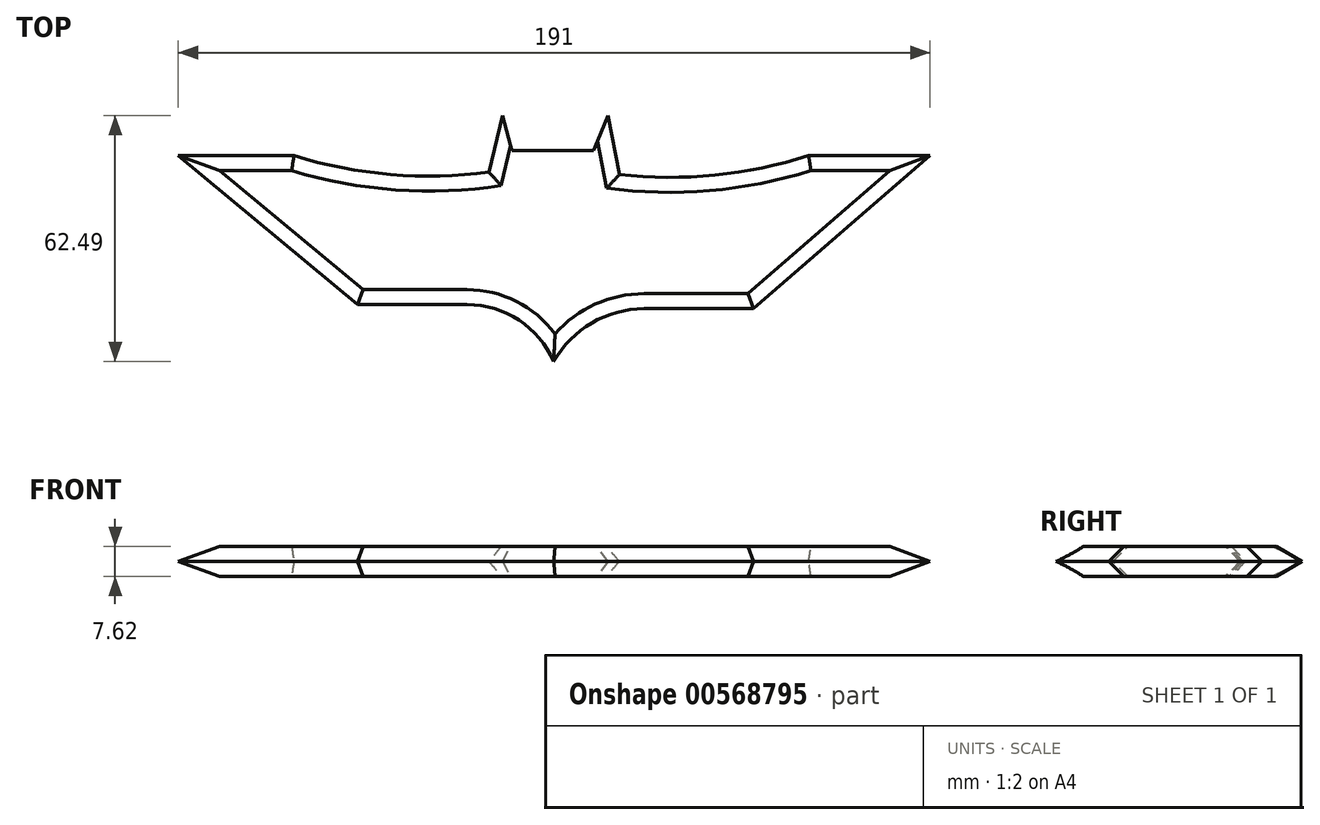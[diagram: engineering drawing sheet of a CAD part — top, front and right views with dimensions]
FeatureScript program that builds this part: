
annotation { "Feature Type Name" : "Feature", "Feature Type Description" : "" }
export const myFeature = defineFeature(function(context is Context, id is Id, definition is map)
    precondition{}
    {
        {
            var Q0;
            Q0=qCreatedBy(makeId("Top.planeOp"),FACE);
            var sketch = newSketch(context, id + "F0", { "sketchPlane" : qUnion([Q0])});
            skLineSegment(sketch, "E0", {"start": v(0, 0) * mm, "end": v(10.36, 0) * mm});
            skLineSegment(sketch, "E1", {"start": v(10.36, 0) * mm, "end": v(0, 0) * mm});
            skLineSegment(sketch, "E2", {"start": v(0, 0) * mm, "end": v(-10.36, 0) * mm});
            skLineSegment(sketch, "E3", {"start": v(-10.36, 0) * mm, "end": v(-13.53, 11.51) * mm});
            skLineSegment(sketch, "E4", {"start": v(10.36, 0) * mm, "end": v(14.85, 11.06) * mm});
            skLineSegment(sketch, "E5", {"start": v(-13.53, 11.51) * mm, "end": v(-17.27, -4.32) * mm});
            skLineSegment(sketch, "E6", {"start": v(14.85, 11.06) * mm, "end": v(17.91, -4.9) * mm});
            skPoint(sketch, "E7.end.orphan", {"position": v(-65.62, 0) * mm});
            skArc(sketch, "E8", {"start": v(-65.62, 0) * mm, "mid": v(-41.67, -4.7) * mm, "end": v(-17.27, -4.32) * mm});
            skArc(sketch, "E9", {"start": v(17.91, -4.9) * mm, "mid": v(41.59, -4.85) * mm, "end": v(64.76, 0) * mm});
            skLineSegment(sketch, "E10", {"start": v(-65.62, 0) * mm, "end": v(-99.3, 0) * mm});
            skLineSegment(sketch, "E11", {"start": v(64.76, 0) * mm, "end": v(99.31, 0) * mm});
            skSolve(sketch);
        }
        {
            var Q0;
            Q0=qCreatedBy(makeId("Top.planeOp"),FACE);
            var sketch = newSketch(context, id + "F1", { "sketchPlane" : qUnion([Q0])});
            skLineSegment(sketch, "E12", {"start": v(-98.72, 0) * mm, "end": v(-50.08, -40.36) * mm});
            skLineSegment(sketch, "E13", {"start": v(-50.08, -40.36) * mm, "end": v(-21.8, -40.36) * mm});
            skLineSegment(sketch, "E14", {"start": v(99.2, 0) * mm, "end": v(51.44, -41.4) * mm});
            skLineSegment(sketch, "E15", {"start": v(51.44, -41.4) * mm, "end": v(23.17, -41.4) * mm});
            skArc(sketch, "E16", {"start": v(0, -56.78) * mm, "mid": v(-8.15, -44.93) * mm, "end": v(-21.8, -40.36) * mm});
            skArc(sketch, "E17", {"start": v(23.17, -41.4) * mm, "mid": v(9.26, -45.6) * mm, "end": v(0, -56.78) * mm});
            skSolve(sketch);
        }
        {
            var Q0;
            Q0=qCreatedBy(makeId("Top.planeOp"),FACE);
            var sketch = newSketch(context, id + "F2", { "sketchPlane" : qUnion([Q0])});
            skLineSegment(sketch, "E18.0", {"start": v(99.2, 0) * mm, "end": v(51.44, -41.4) * mm});
            skLineSegment(sketch, "E18.1", {"start": v(51.44, -41.4) * mm, "end": v(23.17, -41.4) * mm});
            skArc(sketch, "E18.2", {"start": v(23.17, -41.4) * mm, "mid": v(9.26, -45.6) * mm, "end": v(0, -56.78) * mm});
            skArc(sketch, "E18.3", {"start": v(0, -56.78) * mm, "mid": v(-8.15, -44.93) * mm, "end": v(-21.8, -40.36) * mm});
            skLineSegment(sketch, "E18.4", {"start": v(-50.08, -40.36) * mm, "end": v(-21.8, -40.36) * mm});
            skLineSegment(sketch, "E18.5", {"start": v(-98.72, 0) * mm, "end": v(-50.08, -40.36) * mm});
            skLineSegment(sketch, "E18.6", {"start": v(-65.62, 0) * mm, "end": v(-99.3, 0) * mm});
            skArc(sketch, "E18.7", {"start": v(-65.62, 0) * mm, "mid": v(-41.67, -4.7) * mm, "end": v(-17.27, -4.32) * mm});
            skLineSegment(sketch, "E18.8", {"start": v(-13.53, 11.51) * mm, "end": v(-17.27, -4.32) * mm});
            skLineSegment(sketch, "E18.9", {"start": v(-10.36, 0) * mm, "end": v(-13.53, 11.51) * mm});
            skLineSegment(sketch, "E18.10", {"start": v(0, 0) * mm, "end": v(-10.36, 0) * mm});
            skLineSegment(sketch, "E18.11", {"start": v(10.36, 0) * mm, "end": v(0, 0) * mm});
            skLineSegment(sketch, "E18.12", {"start": v(10.36, 0) * mm, "end": v(14.85, 11.06) * mm});
            skLineSegment(sketch, "E18.13", {"start": v(14.85, 11.06) * mm, "end": v(17.91, -4.9) * mm});
            skArc(sketch, "E18.14", {"start": v(17.91, -4.9) * mm, "mid": v(41.59, -4.85) * mm, "end": v(64.76, 0) * mm});
            skLineSegment(sketch, "E18.15", {"start": v(64.76, 0) * mm, "end": v(99.31, 0) * mm});
            skSolve(sketch);
        }
        {
            var Q0;
            Q0 = qSketchRegion(id + "F2", true);
            extrude(context, id + "F3", {"entities" : qUnion([Q0]), "depth" : 7.62 * mm, "offsetDistance" : 25.4 * mm});
        }
        {
            var Q0;
            Q0=makeQuery(id+"F3.opExtrude","CAP_EDGE",EDGE,{"disambiguationData":[OSD([sQuery(id+"F2.wireOp",EDGE,"E18.1")])],"isStart":true});
            var Q1;
            Q1=makeQuery(id+"F3.opExtrude","CAP_EDGE",EDGE,{"disambiguationData":[OSD([sQuery(id+"F2.wireOp",EDGE,"E18.0")])],"isStart":true});
            var Q2;
            Q2=makeQuery(id+"F3.opExtrude","CAP_EDGE",EDGE,{"disambiguationData":[OSD([sQuery(id+"F2.wireOp",EDGE,"E18.15")])],"isStart":true});
            chamfer(context, id + "F4", {"entities" : qUnion([Q0, Q1, Q2]), "width" : 5.08 * mm, "tangentPropagation" : true});
        }
        {
            var Q0;
            Q0=makeQuery(id+"F3.opExtrude","CAP_EDGE",EDGE,{"disambiguationData":[OSD([sQuery(id+"F2.wireOp",EDGE,"E18.15")])],"isStart":false});
            var Q1;
            Q1=makeQuery(id+"F3.opExtrude","CAP_EDGE",EDGE,{"disambiguationData":[OSD([sQuery(id+"F2.wireOp",EDGE,"E18.0")])],"isStart":false});
            chamfer(context, id + "F5", {"entities" : qUnion([Q0, Q1]), "width" : 5.08 * mm, "tangentPropagation" : true});
        }
        {
            var Q0;
            Q0=makeQuery(id+"F3.opExtrude","CAP_EDGE",EDGE,{"disambiguationData":[OSD([sQuery(id+"F2.wireOp",EDGE,"E18.6")])],"isStart":true});
            var Q1;
            Q1=makeQuery(id+"F3.opExtrude","CAP_EDGE",EDGE,{"disambiguationData":[OSD([sQuery(id+"F2.wireOp",EDGE,"E18.6")])],"isStart":false});
            chamfer(context, id + "F6", {"entities" : qUnion([Q0, Q1]), "width" : 5.08 * mm, "tangentPropagation" : true});
        }
        {
            var Q0;
            Q0=makeQuery(id+"F3.opExtrude","CAP_EDGE",EDGE,{"disambiguationData":[OSD([sQuery(id+"F2.wireOp",EDGE,"E18.5")])],"isStart":false});
            chamfer(context, id + "F7", {"entities" : qUnion([Q0]), "width" : 5.08 * mm, "tangentPropagation" : true});
        }
        {
            var Q0;
            Q0=makeQuery(id+"F3.opExtrude","CAP_EDGE",EDGE,{"disambiguationData":[OSD([sQuery(id+"F2.wireOp",EDGE,"E18.5")])],"isStart":true});
            chamfer(context, id + "F8", {"entities" : qUnion([Q0]), "width" : 5.08 * mm, "tangentPropagation" : true});
        }
        {
            var Q0;
            Q0=makeQuery(id+"F3.opExtrude","CAP_EDGE",EDGE,{"disambiguationData":[OSD([sQuery(id+"F2.wireOp",EDGE,"E18.3")])],"isStart":false});
            var Q1;
            Q1=makeQuery(id+"F3.opExtrude","CAP_EDGE",EDGE,{"disambiguationData":[OSD([sQuery(id+"F2.wireOp",EDGE,"E18.2")])],"isStart":false});
            chamfer(context, id + "F9", {"entities" : qUnion([Q0, Q1]), "width" : 5.08 * mm, "tangentPropagation" : true});
        }
        {
            var Q0;
            Q0=makeQuery(id+"F3.opExtrude","CAP_EDGE",EDGE,{"disambiguationData":[OSD([sQuery(id+"F2.wireOp",EDGE,"E18.7")])],"isStart":false});
            var Q1;
            Q1=makeQuery(id+"F3.opExtrude","CAP_EDGE",EDGE,{"disambiguationData":[OSD([sQuery(id+"F2.wireOp",EDGE,"E18.14")])],"isStart":false});
            chamfer(context, id + "F10", {"entities" : qUnion([Q0, Q1]), "width" : 5.08 * mm, "tangentPropagation" : true});
        }
        {
            var Q0;
            Q0=makeQuery(id+"F3.opExtrude","CAP_EDGE",EDGE,{"disambiguationData":[OSD([sQuery(id+"F2.wireOp",EDGE,"E18.13")])],"isStart":false});
            var Q1;
            Q1=makeQuery(id+"F3.opExtrude","CAP_EDGE",EDGE,{"disambiguationData":[OSD([sQuery(id+"F2.wireOp",EDGE,"E18.8")])],"isStart":false});
            chamfer(context, id + "F11", {"entities" : qUnion([Q0, Q1]), "width" : 5.08 * mm, "tangentPropagation" : true});
        }
        {
            var Q0;
            Q0=makeQuery(id+"F3.opExtrude","CAP_EDGE",EDGE,{"disambiguationData":[OSD([sQuery(id+"F2.wireOp",EDGE,"E18.7")])],"isStart":true});
            var Q1;
            Q1=makeQuery(id+"F3.opExtrude","CAP_EDGE",EDGE,{"disambiguationData":[OSD([sQuery(id+"F2.wireOp",EDGE,"E18.14")])],"isStart":true});
            var Q2;
            Q2=makeQuery(id+"F3.opExtrude","CAP_EDGE",EDGE,{"disambiguationData":[OSD([sQuery(id+"F2.wireOp",EDGE,"E18.13")])],"isStart":true});
            var Q3;
            Q3=makeQuery(id+"F3.opExtrude","CAP_EDGE",EDGE,{"disambiguationData":[OSD([sQuery(id+"F2.wireOp",EDGE,"E18.8")])],"isStart":true});
            chamfer(context, id + "F12", {"entities" : qUnion([Q0, Q1, Q2, Q3]), "width" : 5.08 * mm, "tangentPropagation" : true});
        }
        {
            var Q0;
            Q0=makeQuery(id+"F3.opExtrude","CAP_EDGE",EDGE,{"disambiguationData":[OSD([sQuery(id+"F2.wireOp",EDGE,"E18.3")])],"isStart":true});
            chamfer(context, id + "F13", {"entities" : qUnion([Q0]), "width" : 5.08 * mm, "tangentPropagation" : true});
        }
    });
